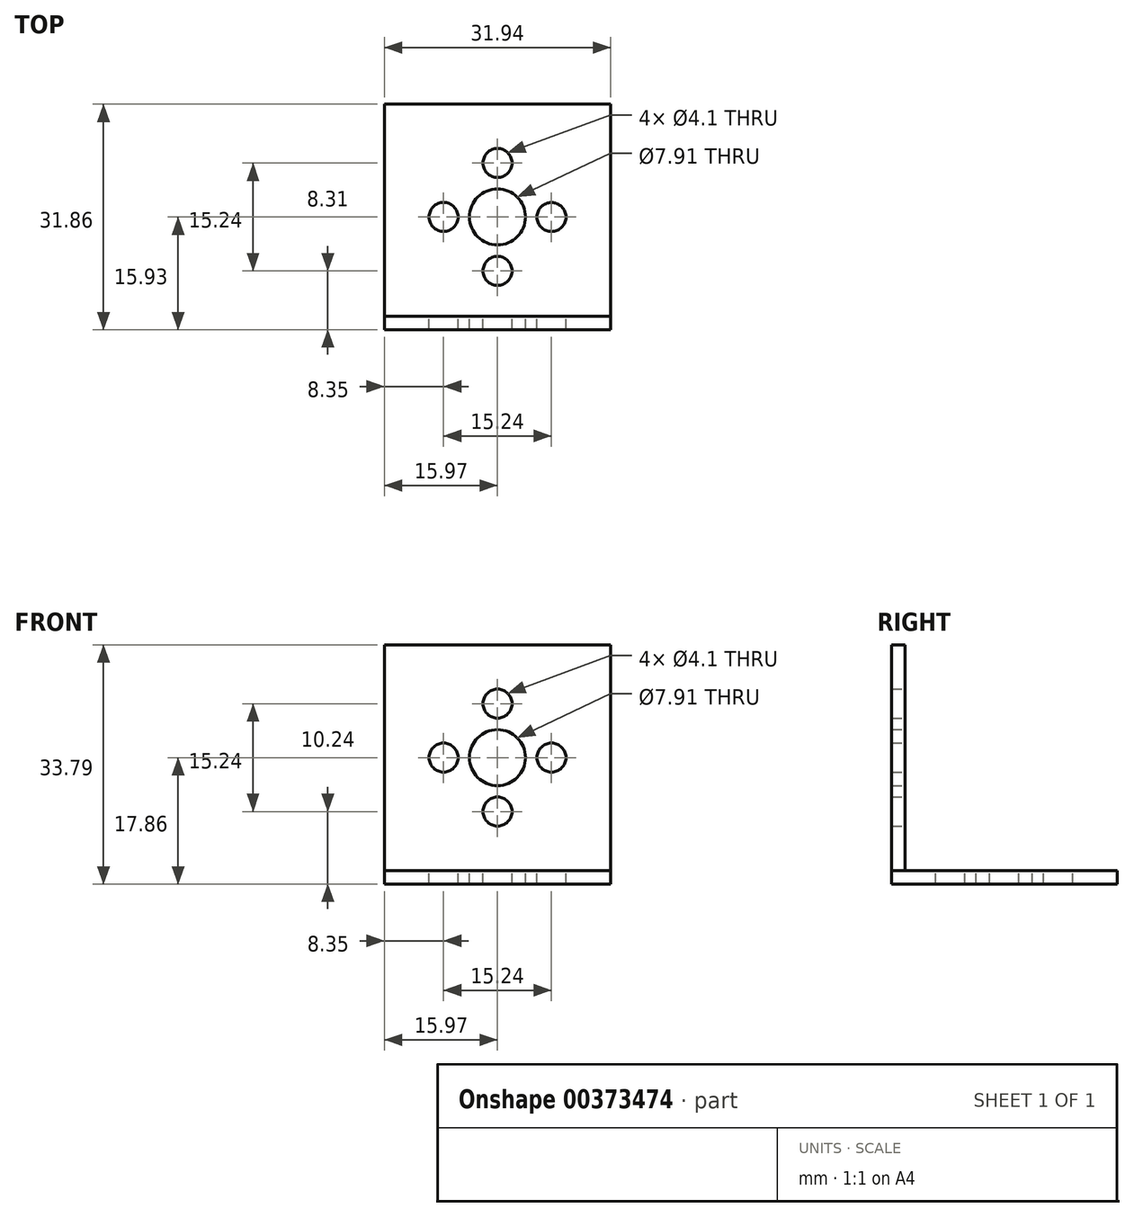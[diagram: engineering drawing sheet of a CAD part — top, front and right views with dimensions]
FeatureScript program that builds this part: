
annotation { "Feature Type Name" : "Feature", "Feature Type Description" : "" }
export const myFeature = defineFeature(function(context is Context, id is Id, definition is map)
    precondition{}
    {
        {
            var Q0;
            Q0=qCreatedBy(makeId("Front.planeOp"),FACE);
            var sketch = newSketch(context, id + "F0", { "sketchPlane" : qUnion([Q0])});
            skLineSegment(sketch, "E0.bottom", {"start": v(15.98, -15.93) * mm, "end": v(-15.97, -15.93) * mm});
            skLineSegment(sketch, "E0.top", {"start": v(15.97, 15.93) * mm, "end": v(-15.98, 15.93) * mm});
            skLineSegment(sketch, "E0.left", {"start": v(15.98, -15.93) * mm, "end": v(15.97, 15.93) * mm});
            skLineSegment(sketch, "E0.right", {"start": v(-15.97, -15.93) * mm, "end": v(-15.98, 15.93) * mm});
            skPoint(sketch, "E0.middle", {"position": v(0, 0) * mm});
            skCircle(sketch, "E1", {"center": v(0, 0) * mm, "radius": 3.96 * mm});
            skCircle(sketch, "E2", {"center": v(0, 7.62) * mm, "radius": 2.05 * mm});
            skCircle(sketch, "E3", {"center": v(-7.62, 0) * mm, "radius": 2.05 * mm});
            skCircle(sketch, "E4", {"center": v(0, -7.62) * mm, "radius": 2.05 * mm});
            skCircle(sketch, "E5", {"center": v(7.62, 0) * mm, "radius": 2.05 * mm});
            skSolve(sketch);
        }
        {
            var Q0;
            Q0=makeQuery(id+"F0.imprint","IMPRINT",FACE,{"disambiguationData":[TD([[makeQuery(id+"F0.imprint","IMPRINT",EDGE,{"derivedFrom":sQuery(id+"F0.wireOp",EDGE,"E0.bottom")}),-1.0]])]});
            extrude(context, id + "F1", {"entities" : qUnion([Q0]), "depth" : 1.93 * mm});
        }
        {
            var Q0;
            Q0=makeQuery(id+"F1.opExtrude","SWEPT_FACE",FACE,{"disambiguationData":[OSD([sQuery(id+"F0.wireOp",EDGE,"E0.bottom")])]});
            var sketch = newSketch(context, id + "F2", { "sketchPlane" : qUnion([Q0])});
            skLineSegment(sketch, "E6.bottom", {"start": v(15.98, -29.93) * mm, "end": v(-15.97, -29.93) * mm});
            skLineSegment(sketch, "E6.top", {"start": v(15.98, 1.93) * mm, "end": v(-15.97, 1.93) * mm});
            skLineSegment(sketch, "E6.left", {"start": v(15.98, -29.93) * mm, "end": v(15.98, 1.93) * mm});
            skLineSegment(sketch, "E6.right", {"start": v(-15.97, -29.93) * mm, "end": v(-15.97, 1.93) * mm});
            skPoint(sketch, "E6.middle", {"position": v(0, -14) * mm});
            skCircle(sketch, "E7", {"center": v(0, -14) * mm, "radius": 3.96 * mm});
            skCircle(sketch, "E8", {"center": v(0, -6.38) * mm, "radius": 2.05 * mm});
            skCircle(sketch, "E9", {"center": v(-7.62, -14) * mm, "radius": 2.05 * mm});
            skCircle(sketch, "E10", {"center": v(0, -21.62) * mm, "radius": 2.05 * mm});
            skCircle(sketch, "E11", {"center": v(7.62, -14) * mm, "radius": 2.05 * mm});
            skSolve(sketch);
        }
        {
            var Q0;
            Q0 = qSketchRegion(id + "F2", true);
            extrude(context, id + "F3", {"entities" : qUnion([Q0]), "depth" : 1.93 * mm});
        }
    });
